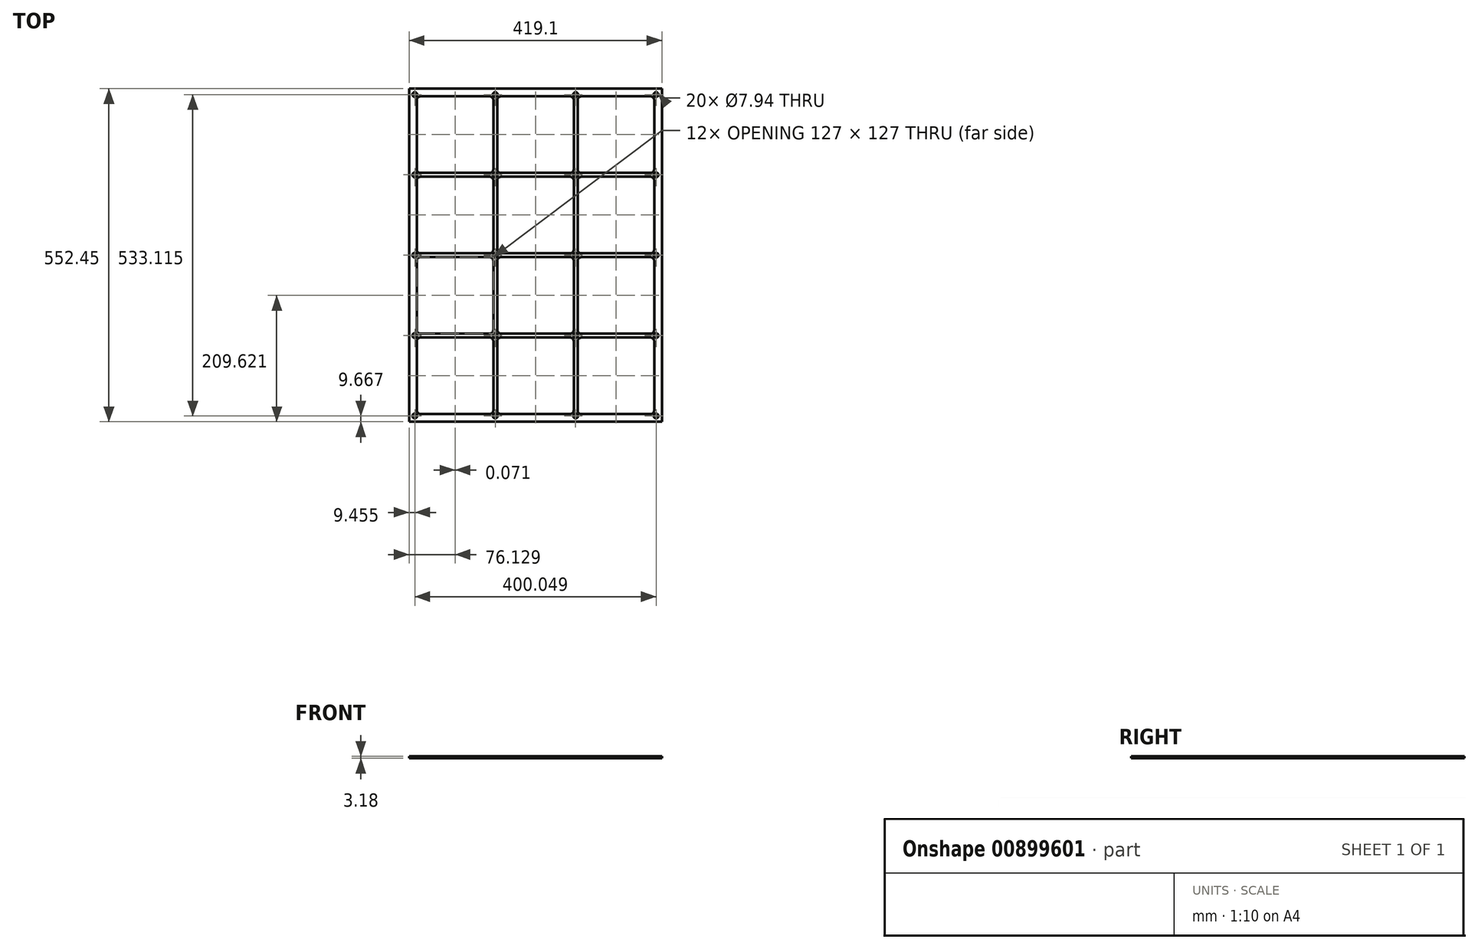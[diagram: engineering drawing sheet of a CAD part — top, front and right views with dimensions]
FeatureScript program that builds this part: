
annotation { "Feature Type Name" : "Feature", "Feature Type Description" : "" }
export const myFeature = defineFeature(function(context is Context, id is Id, definition is map)
    precondition{}
    {
        {
            var Q0;
            Q0=qCreatedBy(makeId("Top.planeOp"),FACE);
            var sketch = newSketch(context, id + "F0", { "sketchPlane" : qUnion([Q0])});
            skLineSegment(sketch, "E0.bottom", {"start": v(19.05, 12.84) * mm, "end": v(133.35, 12.84) * mm});
            skLineSegment(sketch, "E0.top", {"start": v(19.05, 139.84) * mm, "end": v(133.35, 139.84) * mm});
            skLineSegment(sketch, "E0.left", {"start": v(12.7, 19.2) * mm, "end": v(12.7, 133.5) * mm});
            skLineSegment(sketch, "E0.right", {"start": v(139.7, 19.2) * mm, "end": v(139.7, 133.5) * mm});
            skArc(sketch, "E1.filletArc", {"start": v(19.05, 139.84) * mm, "mid": v(14.56, 137.98) * mm, "end": v(12.7, 133.5) * mm});
            skArc(sketch, "E2.filletArc", {"start": v(139.7, 133.5) * mm, "mid": v(137.84, 137.98) * mm, "end": v(133.35, 139.84) * mm});
            skArc(sketch, "E3.filletArc", {"start": v(133.35, 12.84) * mm, "mid": v(137.84, 14.7) * mm, "end": v(139.7, 19.2) * mm});
            skArc(sketch, "E4.filletArc", {"start": v(12.7, 19.2) * mm, "mid": v(14.56, 14.7) * mm, "end": v(19.05, 12.84) * mm});
            skLineSegment(sketch, "E5.0.1.1", {"start": v(139.63, 152.47) * mm, "end": v(139.63, 266.77) * mm});
            skLineSegment(sketch, "E5.0.1.2", {"start": v(18.98, 146.12) * mm, "end": v(133.28, 146.12) * mm});
            skLineSegment(sketch, "E5.0.1.4", {"start": v(18.98, 273.12) * mm, "end": v(133.28, 273.12) * mm});
            skLineSegment(sketch, "E5.0.1.5", {"start": v(12.63, 152.47) * mm, "end": v(12.63, 266.77) * mm});
            skArc(sketch, "E5.0.1.8", {"start": v(139.63, 266.77) * mm, "mid": v(137.77, 271.26) * mm, "end": v(133.28, 273.12) * mm});
            skArc(sketch, "E5.0.1.9", {"start": v(18.98, 273.12) * mm, "mid": v(14.49, 271.26) * mm, "end": v(12.63, 266.77) * mm});
            skArc(sketch, "E5.0.1.10", {"start": v(12.63, 152.47) * mm, "mid": v(14.49, 147.98) * mm, "end": v(18.98, 146.12) * mm});
            skArc(sketch, "E5.0.1.11", {"start": v(133.28, 146.12) * mm, "mid": v(137.77, 147.98) * mm, "end": v(139.63, 152.47) * mm});
            skLineSegment(sketch, "E5.0.2.1", {"start": v(139.7, 285.75) * mm, "end": v(139.7, 400.05) * mm});
            skLineSegment(sketch, "E5.0.2.2", {"start": v(19.05, 279.4) * mm, "end": v(133.35, 279.4) * mm});
            skLineSegment(sketch, "E5.0.2.4", {"start": v(19.05, 406.4) * mm, "end": v(133.35, 406.4) * mm});
            skLineSegment(sketch, "E5.0.2.5", {"start": v(12.7, 285.75) * mm, "end": v(12.7, 400.05) * mm});
            skArc(sketch, "E5.0.2.8", {"start": v(139.7, 400.05) * mm, "mid": v(137.84, 404.54) * mm, "end": v(133.35, 406.4) * mm});
            skArc(sketch, "E5.0.2.9", {"start": v(19.05, 406.4) * mm, "mid": v(14.56, 404.54) * mm, "end": v(12.7, 400.05) * mm});
            skArc(sketch, "E5.0.2.10", {"start": v(12.7, 285.75) * mm, "mid": v(14.56, 281.26) * mm, "end": v(19.05, 279.4) * mm});
            skArc(sketch, "E5.0.2.11", {"start": v(133.35, 279.4) * mm, "mid": v(137.84, 281.26) * mm, "end": v(139.7, 285.75) * mm});
            skLineSegment(sketch, "E5.0.3.1", {"start": v(139.7, 419.1) * mm, "end": v(139.7, 533.4) * mm});
            skLineSegment(sketch, "E5.0.3.2", {"start": v(19.05, 412.75) * mm, "end": v(133.35, 412.75) * mm});
            skLineSegment(sketch, "E5.0.3.4", {"start": v(19.05, 539.75) * mm, "end": v(133.35, 539.75) * mm});
            skLineSegment(sketch, "E5.0.3.5", {"start": v(12.7, 419.1) * mm, "end": v(12.7, 533.4) * mm});
            skArc(sketch, "E5.0.3.8", {"start": v(139.7, 533.4) * mm, "mid": v(137.84, 537.9) * mm, "end": v(133.35, 539.75) * mm});
            skArc(sketch, "E5.0.3.9", {"start": v(19.05, 539.75) * mm, "mid": v(14.56, 537.9) * mm, "end": v(12.7, 533.4) * mm});
            skArc(sketch, "E5.0.3.10", {"start": v(12.7, 419.1) * mm, "mid": v(14.56, 414.6) * mm, "end": v(19.05, 412.75) * mm});
            skArc(sketch, "E5.0.3.11", {"start": v(133.35, 412.75) * mm, "mid": v(137.84, 414.6) * mm, "end": v(139.7, 419.1) * mm});
            skLineSegment(sketch, "E5.1.0.1", {"start": v(272.98, 19.12) * mm, "end": v(272.98, 133.42) * mm});
            skLineSegment(sketch, "E5.1.0.2", {"start": v(152.33, 12.77) * mm, "end": v(266.63, 12.77) * mm});
            skLineSegment(sketch, "E5.1.0.4", {"start": v(152.33, 139.77) * mm, "end": v(266.63, 139.77) * mm});
            skLineSegment(sketch, "E5.1.0.5", {"start": v(145.98, 19.12) * mm, "end": v(145.98, 133.42) * mm});
            skArc(sketch, "E5.1.0.8", {"start": v(272.98, 133.42) * mm, "mid": v(271.12, 137.91) * mm, "end": v(266.63, 139.77) * mm});
            skArc(sketch, "E5.1.0.9", {"start": v(152.33, 139.77) * mm, "mid": v(147.84, 137.91) * mm, "end": v(145.98, 133.42) * mm});
            skArc(sketch, "E5.1.0.10", {"start": v(145.98, 19.12) * mm, "mid": v(147.84, 14.63) * mm, "end": v(152.33, 12.77) * mm});
            skArc(sketch, "E5.1.0.11", {"start": v(266.63, 12.77) * mm, "mid": v(271.12, 14.63) * mm, "end": v(272.98, 19.12) * mm});
            skLineSegment(sketch, "E5.1.1.1", {"start": v(273.05, 152.54) * mm, "end": v(273.05, 266.84) * mm});
            skLineSegment(sketch, "E5.1.1.2", {"start": v(152.4, 146.2) * mm, "end": v(266.7, 146.2) * mm});
            skLineSegment(sketch, "E5.1.1.4", {"start": v(152.4, 273.2) * mm, "end": v(266.7, 273.2) * mm});
            skLineSegment(sketch, "E5.1.1.5", {"start": v(146.05, 152.54) * mm, "end": v(146.05, 266.84) * mm});
            skArc(sketch, "E5.1.1.8", {"start": v(273.05, 266.84) * mm, "mid": v(271.2, 271.33) * mm, "end": v(266.7, 273.2) * mm});
            skArc(sketch, "E5.1.1.9", {"start": v(152.4, 273.2) * mm, "mid": v(147.9, 271.33) * mm, "end": v(146.05, 266.84) * mm});
            skArc(sketch, "E5.1.1.10", {"start": v(146.05, 152.54) * mm, "mid": v(147.9, 148.05) * mm, "end": v(152.4, 146.2) * mm});
            skArc(sketch, "E5.1.1.11", {"start": v(266.7, 146.2) * mm, "mid": v(271.2, 148.05) * mm, "end": v(273.05, 152.54) * mm});
            skLineSegment(sketch, "E5.1.2.1", {"start": v(273.05, 285.75) * mm, "end": v(273.05, 400.05) * mm});
            skLineSegment(sketch, "E5.1.2.2", {"start": v(152.4, 279.4) * mm, "end": v(266.7, 279.4) * mm});
            skLineSegment(sketch, "E5.1.2.4", {"start": v(152.4, 406.4) * mm, "end": v(266.7, 406.4) * mm});
            skLineSegment(sketch, "E5.1.2.5", {"start": v(146.05, 285.75) * mm, "end": v(146.05, 400.05) * mm});
            skArc(sketch, "E5.1.2.8", {"start": v(273.05, 400.05) * mm, "mid": v(271.2, 404.54) * mm, "end": v(266.7, 406.4) * mm});
            skArc(sketch, "E5.1.2.9", {"start": v(152.4, 406.4) * mm, "mid": v(147.9, 404.54) * mm, "end": v(146.05, 400.05) * mm});
            skArc(sketch, "E5.1.2.10", {"start": v(146.05, 285.75) * mm, "mid": v(147.9, 281.26) * mm, "end": v(152.4, 279.4) * mm});
            skArc(sketch, "E5.1.2.11", {"start": v(266.7, 279.4) * mm, "mid": v(271.2, 281.26) * mm, "end": v(273.05, 285.75) * mm});
            skLineSegment(sketch, "E5.1.3.1", {"start": v(273.05, 419.1) * mm, "end": v(273.05, 533.4) * mm});
            skLineSegment(sketch, "E5.1.3.2", {"start": v(152.4, 412.75) * mm, "end": v(266.7, 412.75) * mm});
            skLineSegment(sketch, "E5.1.3.4", {"start": v(152.4, 539.75) * mm, "end": v(266.7, 539.75) * mm});
            skLineSegment(sketch, "E5.1.3.5", {"start": v(146.05, 419.1) * mm, "end": v(146.05, 533.4) * mm});
            skArc(sketch, "E5.1.3.8", {"start": v(273.05, 533.4) * mm, "mid": v(271.2, 537.9) * mm, "end": v(266.7, 539.75) * mm});
            skArc(sketch, "E5.1.3.9", {"start": v(152.4, 539.75) * mm, "mid": v(147.9, 537.9) * mm, "end": v(146.05, 533.4) * mm});
            skArc(sketch, "E5.1.3.10", {"start": v(146.05, 419.1) * mm, "mid": v(147.9, 414.6) * mm, "end": v(152.4, 412.75) * mm});
            skArc(sketch, "E5.1.3.11", {"start": v(266.7, 412.75) * mm, "mid": v(271.2, 414.6) * mm, "end": v(273.05, 419.1) * mm});
            skLineSegment(sketch, "E5.2.0.1", {"start": v(406.4, 19.05) * mm, "end": v(406.4, 133.35) * mm});
            skLineSegment(sketch, "E5.2.0.2", {"start": v(285.75, 12.7) * mm, "end": v(400.05, 12.7) * mm});
            skLineSegment(sketch, "E5.2.0.4", {"start": v(285.75, 139.7) * mm, "end": v(400.05, 139.7) * mm});
            skLineSegment(sketch, "E5.2.0.5", {"start": v(279.4, 19.05) * mm, "end": v(279.4, 133.35) * mm});
            skArc(sketch, "E5.2.0.8", {"start": v(406.4, 133.35) * mm, "mid": v(404.54, 137.84) * mm, "end": v(400.05, 139.7) * mm});
            skArc(sketch, "E5.2.0.9", {"start": v(285.75, 139.7) * mm, "mid": v(281.26, 137.84) * mm, "end": v(279.4, 133.35) * mm});
            skArc(sketch, "E5.2.0.10", {"start": v(279.4, 19.05) * mm, "mid": v(281.26, 14.56) * mm, "end": v(285.75, 12.7) * mm});
            skArc(sketch, "E5.2.0.11", {"start": v(400.05, 12.7) * mm, "mid": v(404.54, 14.56) * mm, "end": v(406.4, 19.05) * mm});
            skLineSegment(sketch, "E5.2.1.1", {"start": v(406.4, 152.4) * mm, "end": v(406.4, 266.7) * mm});
            skLineSegment(sketch, "E5.2.1.2", {"start": v(285.75, 146.05) * mm, "end": v(400.05, 146.05) * mm});
            skLineSegment(sketch, "E5.2.1.4", {"start": v(285.75, 273.05) * mm, "end": v(400.05, 273.05) * mm});
            skLineSegment(sketch, "E5.2.1.5", {"start": v(279.4, 152.4) * mm, "end": v(279.4, 266.7) * mm});
            skArc(sketch, "E5.2.1.8", {"start": v(406.4, 266.7) * mm, "mid": v(404.54, 271.2) * mm, "end": v(400.05, 273.05) * mm});
            skArc(sketch, "E5.2.1.9", {"start": v(285.75, 273.05) * mm, "mid": v(281.26, 271.2) * mm, "end": v(279.4, 266.7) * mm});
            skArc(sketch, "E5.2.1.10", {"start": v(279.4, 152.4) * mm, "mid": v(281.26, 147.9) * mm, "end": v(285.75, 146.05) * mm});
            skArc(sketch, "E5.2.1.11", {"start": v(400.05, 146.05) * mm, "mid": v(404.54, 147.9) * mm, "end": v(406.4, 152.4) * mm});
            skLineSegment(sketch, "E5.2.2.1", {"start": v(406.4, 285.75) * mm, "end": v(406.4, 400.05) * mm});
            skLineSegment(sketch, "E5.2.2.2", {"start": v(285.75, 279.4) * mm, "end": v(400.05, 279.4) * mm});
            skLineSegment(sketch, "E5.2.2.4", {"start": v(285.75, 406.4) * mm, "end": v(400.05, 406.4) * mm});
            skLineSegment(sketch, "E5.2.2.5", {"start": v(279.4, 285.75) * mm, "end": v(279.4, 400.05) * mm});
            skArc(sketch, "E5.2.2.8", {"start": v(406.4, 400.05) * mm, "mid": v(404.54, 404.54) * mm, "end": v(400.05, 406.4) * mm});
            skArc(sketch, "E5.2.2.9", {"start": v(285.75, 406.4) * mm, "mid": v(281.26, 404.54) * mm, "end": v(279.4, 400.05) * mm});
            skArc(sketch, "E5.2.2.10", {"start": v(279.4, 285.75) * mm, "mid": v(281.26, 281.26) * mm, "end": v(285.75, 279.4) * mm});
            skArc(sketch, "E5.2.2.11", {"start": v(400.05, 279.4) * mm, "mid": v(404.54, 281.26) * mm, "end": v(406.4, 285.75) * mm});
            skLineSegment(sketch, "E5.2.3.1", {"start": v(406.4, 419.1) * mm, "end": v(406.4, 533.4) * mm});
            skLineSegment(sketch, "E5.2.3.2", {"start": v(285.75, 412.75) * mm, "end": v(400.05, 412.75) * mm});
            skLineSegment(sketch, "E5.2.3.4", {"start": v(285.75, 539.75) * mm, "end": v(400.05, 539.75) * mm});
            skLineSegment(sketch, "E5.2.3.5", {"start": v(279.4, 419.1) * mm, "end": v(279.4, 533.4) * mm});
            skArc(sketch, "E5.2.3.8", {"start": v(406.4, 533.4) * mm, "mid": v(404.54, 537.9) * mm, "end": v(400.05, 539.75) * mm});
            skArc(sketch, "E5.2.3.9", {"start": v(285.75, 539.75) * mm, "mid": v(281.26, 537.9) * mm, "end": v(279.4, 533.4) * mm});
            skArc(sketch, "E5.2.3.10", {"start": v(279.4, 419.1) * mm, "mid": v(281.26, 414.6) * mm, "end": v(285.75, 412.75) * mm});
            skArc(sketch, "E5.2.3.11", {"start": v(400.05, 412.75) * mm, "mid": v(404.54, 414.6) * mm, "end": v(406.4, 419.1) * mm});
            skLineSegment(sketch, "E6.bottom", {"start": v(0, 0) * mm, "end": v(419.1, 0) * mm});
            skLineSegment(sketch, "E6.top", {"start": v(0, 552.45) * mm, "end": v(419.1, 552.45) * mm});
            skLineSegment(sketch, "E6.left", {"start": v(0, 0) * mm, "end": v(0, 552.45) * mm});
            skLineSegment(sketch, "E6.right", {"start": v(419.1, 0) * mm, "end": v(419.1, 552.45) * mm});
            skLineSegment(sketch, "E7", {"start": v(133.28, 152.47) * mm, "end": v(152.33, 133.42) * mm, "construction": true});
            skLineSegment(sketch, "E8", {"start": v(152.4, 152.54) * mm, "end": v(133.35, 133.5) * mm, "construction": true});
            skLineSegment(sketch, "E9.bottom", {"start": v(13.42, 13.64) * mm, "end": v(5.49, 13.64) * mm, "construction": true});
            skLineSegment(sketch, "E9.top", {"start": v(13.42, 5.7) * mm, "end": v(5.49, 5.7) * mm, "construction": true});
            skLineSegment(sketch, "E9.left", {"start": v(13.42, 13.64) * mm, "end": v(13.42, 5.7) * mm, "construction": true});
            skLineSegment(sketch, "E9.right", {"start": v(5.49, 13.64) * mm, "end": v(5.49, 5.7) * mm, "construction": true});
            skPoint(sketch, "E9.middle", {"position": v(142.8, 142.95) * mm});
            skCircle(sketch, "E10", {"center": v(9.45, 9.67) * mm, "radius": 3.97 * mm});
            skLineSegment(sketch, "E11", {"start": v(266.63, 133.42) * mm, "end": v(285.75, 152.4) * mm, "construction": true});
            skLineSegment(sketch, "E12", {"start": v(285.75, 133.35) * mm, "end": v(266.7, 152.54) * mm, "construction": true});
            skLineSegment(sketch, "E13", {"start": v(133.35, 285.75) * mm, "end": v(152.4, 266.84) * mm, "construction": true});
            skLineSegment(sketch, "E14", {"start": v(133.28, 266.77) * mm, "end": v(152.4, 285.75) * mm, "construction": true});
            skLineSegment(sketch, "E15", {"start": v(266.7, 285.75) * mm, "end": v(285.75, 266.7) * mm, "construction": true});
            skLineSegment(sketch, "E16", {"start": v(285.75, 285.75) * mm, "end": v(266.7, 266.84) * mm, "construction": true});
            skLineSegment(sketch, "E17", {"start": v(142.84, 276.26) * mm, "end": v(276.19, 276.26) * mm, "construction": true});
            skLineSegment(sketch, "E18", {"start": v(276.19, 276.26) * mm, "end": v(276.19, 142.98) * mm, "construction": true});
            skLineSegment(sketch, "E19.0.1.0", {"start": v(13.42, 138.98) * mm, "end": v(5.49, 138.98) * mm, "construction": true});
            skLineSegment(sketch, "E19.0.1.1", {"start": v(13.42, 146.91) * mm, "end": v(5.49, 146.91) * mm, "construction": true});
            skLineSegment(sketch, "E19.0.1.2", {"start": v(5.49, 146.91) * mm, "end": v(5.49, 138.98) * mm, "construction": true});
            skLineSegment(sketch, "E19.0.1.3", {"start": v(13.42, 146.91) * mm, "end": v(13.42, 138.98) * mm, "construction": true});
            skCircle(sketch, "E19.0.1.4", {"center": v(9.45, 142.95) * mm, "radius": 3.97 * mm});
            skLineSegment(sketch, "E19.1.0.0", {"start": v(146.77, 5.7) * mm, "end": v(138.84, 5.7) * mm, "construction": true});
            skLineSegment(sketch, "E19.1.0.1", {"start": v(146.77, 13.64) * mm, "end": v(138.84, 13.64) * mm, "construction": true});
            skLineSegment(sketch, "E19.1.0.2", {"start": v(138.84, 13.64) * mm, "end": v(138.84, 5.7) * mm, "construction": true});
            skLineSegment(sketch, "E19.1.0.3", {"start": v(146.77, 13.64) * mm, "end": v(146.77, 5.7) * mm, "construction": true});
            skCircle(sketch, "E19.1.0.4", {"center": v(142.8, 9.67) * mm, "radius": 3.97 * mm});
            skLineSegment(sketch, "E19.1.1.0", {"start": v(146.77, 138.98) * mm, "end": v(138.84, 138.98) * mm, "construction": true});
            skLineSegment(sketch, "E19.1.1.1", {"start": v(146.77, 146.91) * mm, "end": v(138.84, 146.91) * mm, "construction": true});
            skLineSegment(sketch, "E19.1.1.2", {"start": v(138.84, 146.91) * mm, "end": v(138.84, 138.98) * mm, "construction": true});
            skLineSegment(sketch, "E19.1.1.3", {"start": v(146.77, 146.91) * mm, "end": v(146.77, 138.98) * mm, "construction": true});
            skCircle(sketch, "E19.1.1.4", {"center": v(142.8, 142.95) * mm, "radius": 3.97 * mm});
            skLineSegment(sketch, "E19.2.0.0", {"start": v(280.12, 5.7) * mm, "end": v(272.19, 5.7) * mm, "construction": true});
            skLineSegment(sketch, "E19.2.0.1", {"start": v(280.12, 13.64) * mm, "end": v(272.19, 13.64) * mm, "construction": true});
            skLineSegment(sketch, "E19.2.0.2", {"start": v(272.19, 13.64) * mm, "end": v(272.19, 5.7) * mm, "construction": true});
            skLineSegment(sketch, "E19.2.0.3", {"start": v(280.12, 13.64) * mm, "end": v(280.12, 5.7) * mm, "construction": true});
            skCircle(sketch, "E19.2.0.4", {"center": v(276.15, 9.67) * mm, "radius": 3.97 * mm});
            skLineSegment(sketch, "E19.2.1.0", {"start": v(280.12, 138.98) * mm, "end": v(272.19, 138.98) * mm, "construction": true});
            skLineSegment(sketch, "E19.2.1.1", {"start": v(280.12, 146.91) * mm, "end": v(272.19, 146.91) * mm, "construction": true});
            skLineSegment(sketch, "E19.2.1.2", {"start": v(272.19, 146.91) * mm, "end": v(272.19, 138.98) * mm, "construction": true});
            skLineSegment(sketch, "E19.2.1.3", {"start": v(280.12, 146.91) * mm, "end": v(280.12, 138.98) * mm, "construction": true});
            skCircle(sketch, "E19.2.1.4", {"center": v(276.15, 142.95) * mm, "radius": 3.97 * mm});
            skLineSegment(sketch, "E19.3.0.0", {"start": v(413.47, 5.7) * mm, "end": v(405.54, 5.7) * mm, "construction": true});
            skLineSegment(sketch, "E19.3.0.1", {"start": v(413.47, 13.64) * mm, "end": v(405.54, 13.64) * mm, "construction": true});
            skLineSegment(sketch, "E19.3.0.2", {"start": v(405.54, 13.64) * mm, "end": v(405.54, 5.7) * mm, "construction": true});
            skLineSegment(sketch, "E19.3.0.3", {"start": v(413.47, 13.64) * mm, "end": v(413.47, 5.7) * mm, "construction": true});
            skCircle(sketch, "E19.3.0.4", {"center": v(409.5, 9.67) * mm, "radius": 3.97 * mm});
            skLineSegment(sketch, "E19.3.1.0", {"start": v(413.47, 138.98) * mm, "end": v(405.54, 138.98) * mm, "construction": true});
            skLineSegment(sketch, "E19.3.1.1", {"start": v(413.47, 146.91) * mm, "end": v(405.54, 146.91) * mm, "construction": true});
            skLineSegment(sketch, "E19.3.1.2", {"start": v(405.54, 146.91) * mm, "end": v(405.54, 138.98) * mm, "construction": true});
            skLineSegment(sketch, "E19.3.1.3", {"start": v(413.47, 146.91) * mm, "end": v(413.47, 138.98) * mm, "construction": true});
            skCircle(sketch, "E19.3.1.4", {"center": v(409.5, 142.95) * mm, "radius": 3.97 * mm});
            skLineSegment(sketch, "E20.0.0.2", {"start": v(13.42, 272.26) * mm, "end": v(5.49, 272.26) * mm, "construction": true});
            skLineSegment(sketch, "E20.3.0.2", {"start": v(13.42, 280.2) * mm, "end": v(5.49, 280.2) * mm, "construction": true});
            skLineSegment(sketch, "E20.6.0.2", {"start": v(5.49, 280.2) * mm, "end": v(5.49, 272.26) * mm, "construction": true});
            skLineSegment(sketch, "E20.9.0.2", {"start": v(13.42, 280.2) * mm, "end": v(13.42, 272.26) * mm, "construction": true});
            skCircle(sketch, "E20.12.0.2", {"center": v(9.45, 276.22) * mm, "radius": 3.97 * mm});
            skLineSegment(sketch, "E20.0.0.3", {"start": v(13.42, 405.53) * mm, "end": v(5.49, 405.53) * mm, "construction": true});
            skLineSegment(sketch, "E20.3.0.3", {"start": v(13.42, 413.47) * mm, "end": v(5.49, 413.47) * mm, "construction": true});
            skLineSegment(sketch, "E20.6.0.3", {"start": v(5.49, 413.47) * mm, "end": v(5.49, 405.53) * mm, "construction": true});
            skLineSegment(sketch, "E20.9.0.3", {"start": v(13.42, 413.47) * mm, "end": v(13.42, 405.53) * mm, "construction": true});
            skCircle(sketch, "E20.12.0.3", {"center": v(9.45, 409.5) * mm, "radius": 3.97 * mm});
            skLineSegment(sketch, "E20.0.0.4", {"start": v(13.42, 538.81) * mm, "end": v(5.49, 538.81) * mm, "construction": true});
            skLineSegment(sketch, "E20.3.0.4", {"start": v(13.42, 546.75) * mm, "end": v(5.49, 546.75) * mm, "construction": true});
            skLineSegment(sketch, "E20.6.0.4", {"start": v(5.49, 546.75) * mm, "end": v(5.49, 538.81) * mm, "construction": true});
            skLineSegment(sketch, "E20.9.0.4", {"start": v(13.42, 546.75) * mm, "end": v(13.42, 538.81) * mm, "construction": true});
            skCircle(sketch, "E20.12.0.4", {"center": v(9.45, 542.78) * mm, "radius": 3.97 * mm});
            skLineSegment(sketch, "E20.0.1.2", {"start": v(146.77, 272.26) * mm, "end": v(138.84, 272.26) * mm, "construction": true});
            skLineSegment(sketch, "E20.3.1.2", {"start": v(146.77, 280.2) * mm, "end": v(138.84, 280.2) * mm, "construction": true});
            skLineSegment(sketch, "E20.6.1.2", {"start": v(138.84, 280.2) * mm, "end": v(138.84, 272.26) * mm, "construction": true});
            skLineSegment(sketch, "E20.9.1.2", {"start": v(146.77, 280.2) * mm, "end": v(146.77, 272.26) * mm, "construction": true});
            skCircle(sketch, "E20.12.1.2", {"center": v(142.8, 276.22) * mm, "radius": 3.97 * mm});
            skLineSegment(sketch, "E20.0.1.3", {"start": v(146.77, 405.53) * mm, "end": v(138.84, 405.53) * mm, "construction": true});
            skLineSegment(sketch, "E20.3.1.3", {"start": v(146.77, 413.47) * mm, "end": v(138.84, 413.47) * mm, "construction": true});
            skLineSegment(sketch, "E20.6.1.3", {"start": v(138.84, 413.47) * mm, "end": v(138.84, 405.53) * mm, "construction": true});
            skLineSegment(sketch, "E20.9.1.3", {"start": v(146.77, 413.47) * mm, "end": v(146.77, 405.53) * mm, "construction": true});
            skCircle(sketch, "E20.12.1.3", {"center": v(142.8, 409.5) * mm, "radius": 3.97 * mm});
            skLineSegment(sketch, "E20.0.1.4", {"start": v(146.77, 538.81) * mm, "end": v(138.84, 538.81) * mm, "construction": true});
            skLineSegment(sketch, "E20.3.1.4", {"start": v(146.77, 546.75) * mm, "end": v(138.84, 546.75) * mm, "construction": true});
            skLineSegment(sketch, "E20.6.1.4", {"start": v(138.84, 546.75) * mm, "end": v(138.84, 538.81) * mm, "construction": true});
            skLineSegment(sketch, "E20.9.1.4", {"start": v(146.77, 546.75) * mm, "end": v(146.77, 538.81) * mm, "construction": true});
            skCircle(sketch, "E20.12.1.4", {"center": v(142.8, 542.78) * mm, "radius": 3.97 * mm});
            skLineSegment(sketch, "E20.0.2.2", {"start": v(280.12, 272.26) * mm, "end": v(272.19, 272.26) * mm, "construction": true});
            skLineSegment(sketch, "E20.3.2.2", {"start": v(280.12, 280.2) * mm, "end": v(272.19, 280.2) * mm, "construction": true});
            skLineSegment(sketch, "E20.6.2.2", {"start": v(272.19, 280.2) * mm, "end": v(272.19, 272.26) * mm, "construction": true});
            skLineSegment(sketch, "E20.9.2.2", {"start": v(280.12, 280.2) * mm, "end": v(280.12, 272.26) * mm, "construction": true});
            skCircle(sketch, "E20.12.2.2", {"center": v(276.15, 276.22) * mm, "radius": 3.97 * mm});
            skLineSegment(sketch, "E20.0.2.3", {"start": v(280.12, 405.53) * mm, "end": v(272.19, 405.53) * mm, "construction": true});
            skLineSegment(sketch, "E20.3.2.3", {"start": v(280.12, 413.47) * mm, "end": v(272.19, 413.47) * mm, "construction": true});
            skLineSegment(sketch, "E20.6.2.3", {"start": v(272.19, 413.47) * mm, "end": v(272.19, 405.53) * mm, "construction": true});
            skLineSegment(sketch, "E20.9.2.3", {"start": v(280.12, 413.47) * mm, "end": v(280.12, 405.53) * mm, "construction": true});
            skCircle(sketch, "E20.12.2.3", {"center": v(276.15, 409.5) * mm, "radius": 3.97 * mm});
            skLineSegment(sketch, "E20.0.2.4", {"start": v(280.12, 538.81) * mm, "end": v(272.19, 538.81) * mm, "construction": true});
            skLineSegment(sketch, "E20.3.2.4", {"start": v(280.12, 546.75) * mm, "end": v(272.19, 546.75) * mm, "construction": true});
            skLineSegment(sketch, "E20.6.2.4", {"start": v(272.19, 546.75) * mm, "end": v(272.19, 538.81) * mm, "construction": true});
            skLineSegment(sketch, "E20.9.2.4", {"start": v(280.12, 546.75) * mm, "end": v(280.12, 538.81) * mm, "construction": true});
            skCircle(sketch, "E20.12.2.4", {"center": v(276.15, 542.78) * mm, "radius": 3.97 * mm});
            skLineSegment(sketch, "E20.0.3.2", {"start": v(413.47, 272.26) * mm, "end": v(405.54, 272.26) * mm, "construction": true});
            skLineSegment(sketch, "E20.3.3.2", {"start": v(413.47, 280.2) * mm, "end": v(405.54, 280.2) * mm, "construction": true});
            skLineSegment(sketch, "E20.6.3.2", {"start": v(405.54, 280.2) * mm, "end": v(405.54, 272.26) * mm, "construction": true});
            skLineSegment(sketch, "E20.9.3.2", {"start": v(413.47, 280.2) * mm, "end": v(413.47, 272.26) * mm, "construction": true});
            skCircle(sketch, "E20.12.3.2", {"center": v(409.5, 276.22) * mm, "radius": 3.97 * mm});
            skLineSegment(sketch, "E20.0.3.3", {"start": v(413.47, 405.53) * mm, "end": v(405.54, 405.53) * mm, "construction": true});
            skLineSegment(sketch, "E20.3.3.3", {"start": v(413.47, 413.47) * mm, "end": v(405.54, 413.47) * mm, "construction": true});
            skLineSegment(sketch, "E20.6.3.3", {"start": v(405.54, 413.47) * mm, "end": v(405.54, 405.53) * mm, "construction": true});
            skLineSegment(sketch, "E20.9.3.3", {"start": v(413.47, 413.47) * mm, "end": v(413.47, 405.53) * mm, "construction": true});
            skCircle(sketch, "E20.12.3.3", {"center": v(409.5, 409.5) * mm, "radius": 3.97 * mm});
            skLineSegment(sketch, "E20.0.3.4", {"start": v(413.47, 538.81) * mm, "end": v(405.54, 538.81) * mm, "construction": true});
            skLineSegment(sketch, "E20.3.3.4", {"start": v(413.47, 546.75) * mm, "end": v(405.54, 546.75) * mm, "construction": true});
            skLineSegment(sketch, "E20.6.3.4", {"start": v(405.54, 546.75) * mm, "end": v(405.54, 538.81) * mm, "construction": true});
            skLineSegment(sketch, "E20.9.3.4", {"start": v(413.47, 546.75) * mm, "end": v(413.47, 538.81) * mm, "construction": true});
            skCircle(sketch, "E20.12.3.4", {"center": v(409.5, 542.78) * mm, "radius": 3.97 * mm});
            skSolve(sketch);
        }
        {
            var Q0;
            Q0=makeQuery(id+"F0.imprint","IMPRINT",FACE,{"disambiguationData":[TD([[makeQuery(id+"F0.imprint","IMPRINT",EDGE,{"derivedFrom":sQuery(id+"F0.wireOp",EDGE,"E0.bottom")}),-1.0]])]});
            extrude(context, id + "F1", {"entities" : qUnion([Q0]), "depth" : 3.17 * mm, "offsetDistance" : 25.4 * mm});
        }
    });
